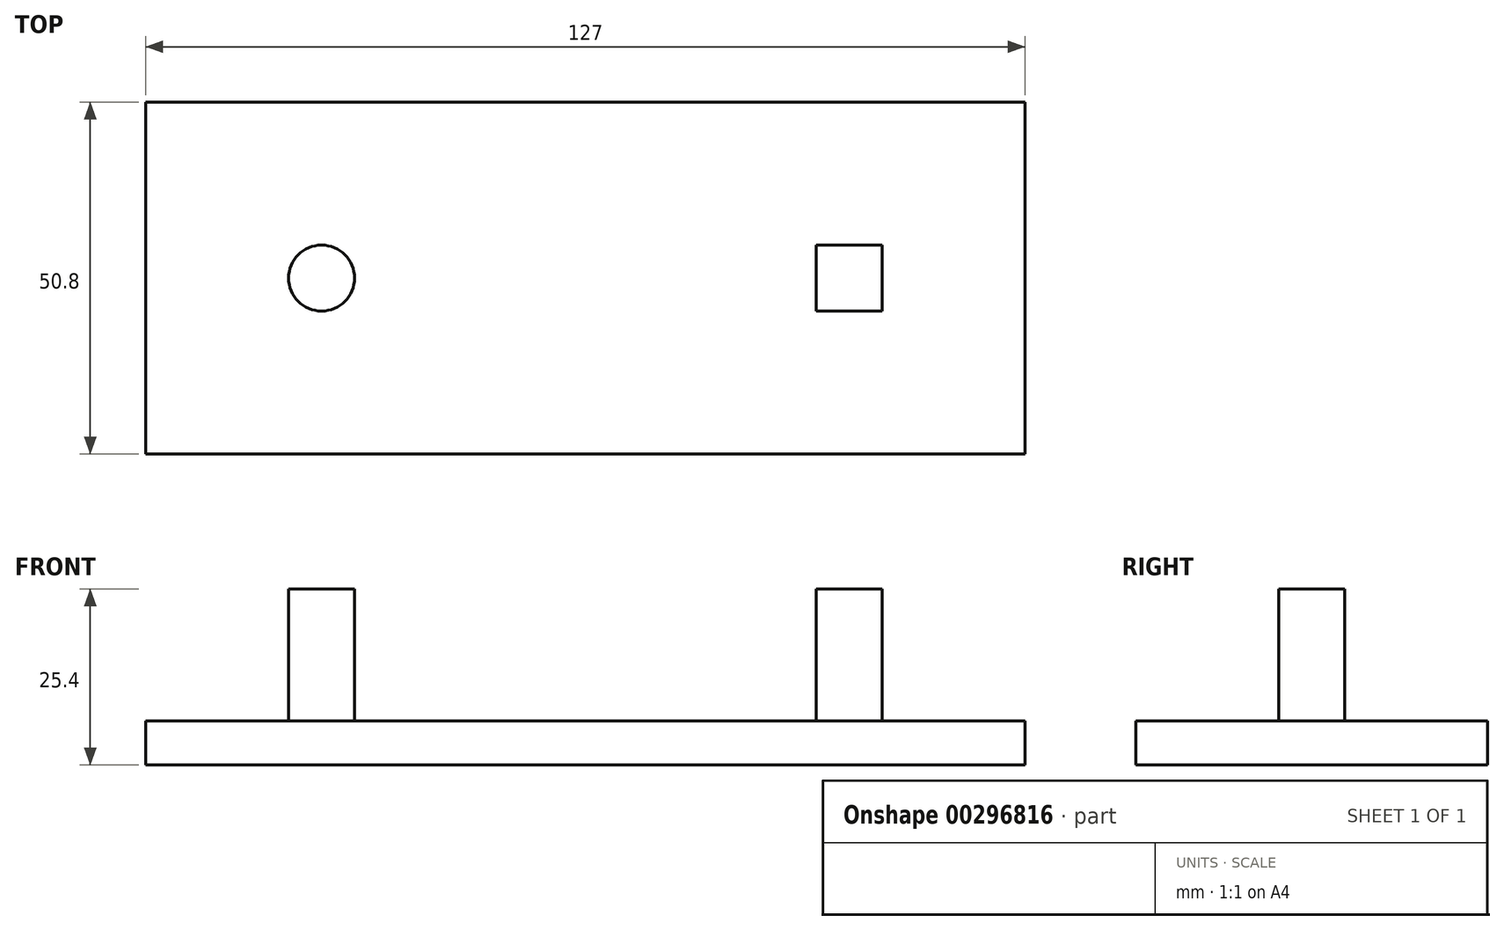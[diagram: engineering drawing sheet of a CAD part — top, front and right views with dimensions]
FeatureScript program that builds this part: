
annotation { "Feature Type Name" : "Feature", "Feature Type Description" : "" }
export const myFeature = defineFeature(function(context is Context, id is Id, definition is map)
    precondition{}
    {
        {
            var Q0;
            Q0=qCreatedBy(makeId("Top.planeOp"),FACE);
            var sketch = newSketch(context, id + "F0", { "sketchPlane" : qUnion([Q0])});
            skLineSegment(sketch, "E0.bottom", {"start": v(-122.89, 17.4) * mm, "end": v(4.11, 17.4) * mm});
            skLineSegment(sketch, "E0.top", {"start": v(-122.89, -33.4) * mm, "end": v(4.11, -33.4) * mm});
            skLineSegment(sketch, "E0.left", {"start": v(-122.89, 17.4) * mm, "end": v(-122.89, -33.4) * mm});
            skLineSegment(sketch, "E0.right", {"start": v(4.11, 17.4) * mm, "end": v(4.11, -33.4) * mm});
            skSolve(sketch);
        }
        {
            var Q0;
            Q0=makeQuery(id+"F0.imprint","IMPRINT",FACE,{"disambiguationData":[TD([[makeQuery(id+"F0.imprint","IMPRINT",EDGE,{"derivedFrom":sQuery(id+"F0.wireOp",EDGE,"E0.bottom")}),-1.0]])]});
            extrude(context, id + "F1", {"entities" : qUnion([Q0]), "depth" : 6.35 * mm});
        }
        {
            var Q0;
            Q0=makeQuery(id+"F1.opExtrude","CAP_FACE",FACE,{"disambiguationData":[OSD([sQuery(id+"F0.wireOp",EDGE,"E0.bottom"),sQuery(id+"F0.wireOp",EDGE,"E0.top"),sQuery(id+"F0.wireOp",EDGE,"E0.left"),sQuery(id+"F0.wireOp",EDGE,"E0.right")])],"isStart":false});
            var sketch = newSketch(context, id + "F2", { "sketchPlane" : qUnion([Q0])});
            skCircle(sketch, "E1", {"center": v(-97.49, -8) * mm, "radius": 4.76 * mm});
            skPoint(sketch, "E1.centerSnap0", {"position": v(4.11, -8) * mm});
            skSolve(sketch);
        }
        {
            var Q0;
            Q0=makeQuery(id+"F2.imprint","IMPRINT",FACE,{"disambiguationData":[TD([[makeQuery(id+"F2.imprint","IMPRINT",EDGE,{"derivedFrom":sQuery(id+"F2.wireOp",EDGE,"E1")}),1.0]])]});
            extrude(context, id + "F3", {"entities" : qUnion([Q0]), "operationType" : NewBodyOperationType.ADD, "depth" : 19.05 * mm});
        }
        {
            var Q0;
            Q0=makeQuery(id+"F1.opExtrude","CAP_FACE",FACE,{"disambiguationData":[OSD([sQuery(id+"F0.wireOp",EDGE,"E0.bottom"),sQuery(id+"F0.wireOp",EDGE,"E0.top"),sQuery(id+"F0.wireOp",EDGE,"E0.left"),sQuery(id+"F0.wireOp",EDGE,"E0.right")])],"isStart":false});
            var sketch = newSketch(context, id + "F4", { "sketchPlane" : qUnion([Q0])});
            skLineSegment(sketch, "E2.bottom", {"start": v(-16.53, -12.76) * mm, "end": v(-26.05, -12.76) * mm});
            skLineSegment(sketch, "E2.top", {"start": v(-16.53, -3.23) * mm, "end": v(-26.05, -3.23) * mm});
            skLineSegment(sketch, "E2.left", {"start": v(-16.53, -12.76) * mm, "end": v(-16.53, -3.23) * mm});
            skLineSegment(sketch, "E2.right", {"start": v(-26.05, -12.76) * mm, "end": v(-26.05, -3.23) * mm});
            skPoint(sketch, "E2.middle", {"position": v(-21.29, -8) * mm});
            skSolve(sketch);
        }
        {
            var Q0;
            Q0=makeQuery(id+"F4.imprint","IMPRINT",FACE,{"disambiguationData":[TD([[makeQuery(id+"F4.imprint","IMPRINT",EDGE,{"derivedFrom":sQuery(id+"F4.wireOp",EDGE,"E2.bottom")}),-1.0]])]});
            extrude(context, id + "F5", {"entities" : qUnion([Q0]), "operationType" : NewBodyOperationType.ADD, "depth" : 19.05 * mm});
        }
    });
